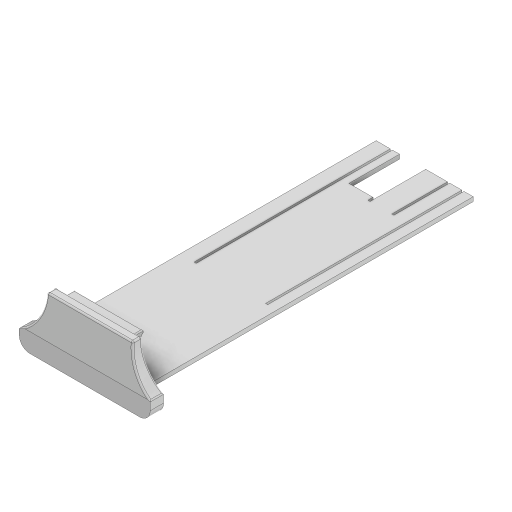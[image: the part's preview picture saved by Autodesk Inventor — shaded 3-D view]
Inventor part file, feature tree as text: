
AUTODESK INVENTOR PART (.ipt)
format: ipt  version: 2024 (Build 280153000, 153)  size: 324,096 bytes
history: native  units: mm
features: extrude x8, sketch x6, chamfer x3, fillet x3
ambient origin geometry x8: Origin, YZ Plane, XZ Plane, XY Plane, X Axis, Y Axis, Z Axis, Center Point
bodies: Solid1 (feature_tree)
feature tree (20):
  sketch  "Sketch1"  dims[d0=46.0mm d1=156.0mm]
  extrude  "Extrusion1"  Depth=156.0mm
  extrude  "Extrusion2"  Depth=6.4mm
  extrude  "Extrusion3"  Depth=93.0mm
  extrude  "Extrusion4"  Depth=24.0mm
  chamfer  "Chamfer1"  Distance=1.0mm
  chamfer  "Chamfer2"  Distance=14.8mm
  extrude  "Extrusion5"  Depth=5.0mm
  extrude  "Extrusion7"  Depth=5.0mm
  extrude  "Extrusion8"  Depth=5.0mm
  extrude  "Extrusion9"  Depth=5.0mm
  chamfer  "Chamfer4"  Distance=2.0mm
  fillet  "Fillet5"  Radius=1.0mm
  fillet  "Fillet6"  Radius=1.0mm
  fillet  "Fillet7"  Radius=1.0mm
  sketch  "Sketch2"  dims[d2=62.0mm d3=6.4mm]
  sketch  "Sketch3"  dims[d4=1.0mm d5=93.0mm]
  sketch  "Sketch5"  dims[d6=6.7mm d7=24.0mm]
  sketch  "Sketch6"  dims[d8=11.4mm]
  sketch  "Sketch8"  dims[d9=2.4mm d10=1.0mm d11=14.8mm d12=1.0mm d13=10.3mm d14=1.0mm d15=5.8mm d16=2.0mm d17=0.0mm d18=1.0mm d19=0.0mm d20=1.0mm d21=1.0mm d22=1.0mm d23=1.0mm d24=1.0mm d25=1.0mm d27=4.0mm d28=0.0mm d29=8.0mm d30=3.0mm d31=3.0mm d32=0.0mm d33=3.0mm d34=2.0mm d35=45.0deg d36=2.0mm d37=2.0mm d38=45.0deg d39=22.0mm d40=5.0mm d41=0.0mm d42=0.0mm d52=32.591mm d53=5.0mm d54=0.0mm d55=0.0mm d56=0.0mm d57=38.3mm d58=9.3mm d63=60.0deg d64=8.0mm d65=120.0deg d66=0.0mm d67=0.0mm d68=18.0mm d69=2.0mm d70=1.22173mm d73=13.4mm d74=13.174311mm d75=1.681761mm d76=1.230725mm d77=0.5mm d78=0.75mm d79=5.0mm d80=5.0mm d81=1.825689mm d47=0.0mm d48=0.0mm d49=0.0mm d50=0.0mm]
